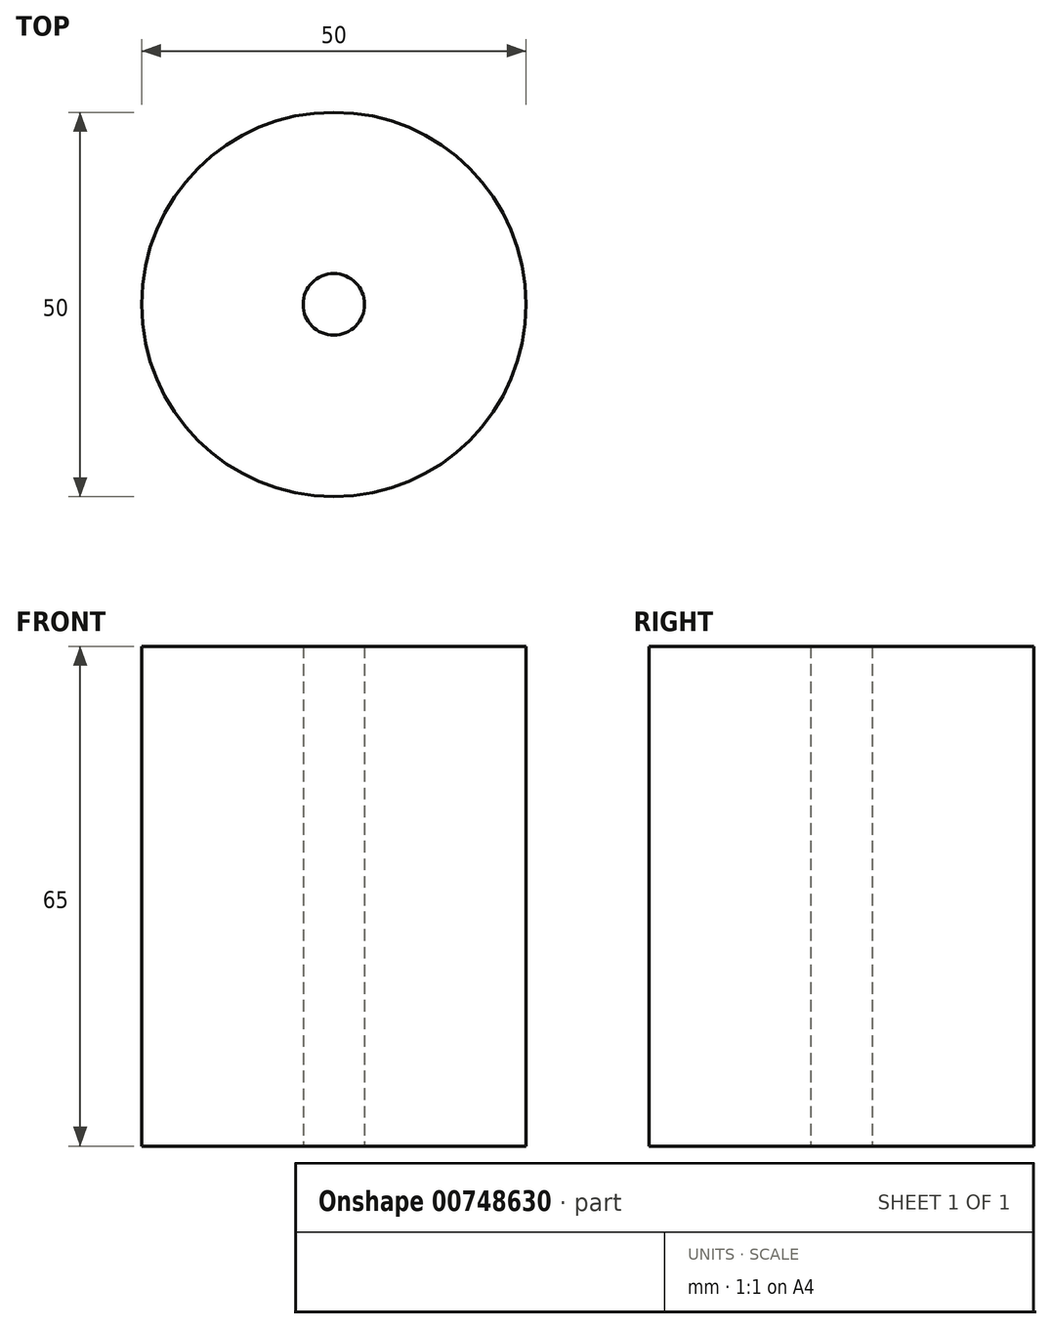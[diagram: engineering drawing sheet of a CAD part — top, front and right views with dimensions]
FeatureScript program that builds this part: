
annotation { "Feature Type Name" : "Feature", "Feature Type Description" : "" }
export const myFeature = defineFeature(function(context is Context, id is Id, definition is map)
    precondition{}
    {
        {
            var Q0;
            Q0=qCreatedBy(makeId("Top.planeOp"),FACE);
            var sketch = newSketch(context, id + "F0", { "sketchPlane" : qUnion([Q0])});
            skCircle(sketch, "E0", {"center": v(0, 0) * mm, "radius": 25 * mm});
            skSolve(sketch);
        }
        {
            var Q0;
            Q0=makeQuery(id+"F0.imprint","IMPRINT",FACE,{"disambiguationData":[TD([[makeQuery(id+"F0.imprint","IMPRINT",EDGE,{"derivedFrom":sQuery(id+"F0.wireOp",EDGE,"E0")}),1.0]])]});
            var Q1;
            Q1=makeQuery(id+"F0.imprint","IMPRINT",FACE,{"disambiguationData":[TD([[makeQuery(id+"F0.imprint","IMPRINT",EDGE,{"derivedFrom":sQuery(id+"F0.wireOp",EDGE,"v6GlskT7-aZC5-e0Fn-29L1-ygovK5jTZAp7")}),1.0]])]});
            extrude(context, id + "F1", {"entities" : qUnion([Q0, Q1]), "depth" : 65 * mm, "offsetDistance" : 25 * mm});
        }
        {
            var Q0;
            Q0=makeQuery(id+"F1.opExtrude","CAP_FACE",FACE,{"disambiguationData":[OSD([sQuery(id+"F0.wireOp",EDGE,"E0")])],"isStart":true});
            var sketch = newSketch(context, id + "F2", { "sketchPlane" : qUnion([Q0])});
            skCircle(sketch, "E1", {"center": v(0, 0) * mm, "radius": 4 * mm});
            skSolve(sketch);
        }
        {
            var Q0;
            Q0=qSketchRegion(id+"F2",true);
            extrude(context, id + "F3", {"entities" : qUnion([Q0]), "operationType" : NewBodyOperationType.REMOVE, "endBound" : BoundingType.THROUGH_ALL, "oppositeDirection" : true, "depth" : 25 * mm, "offsetDistance" : 25 * mm});
        }
    });
